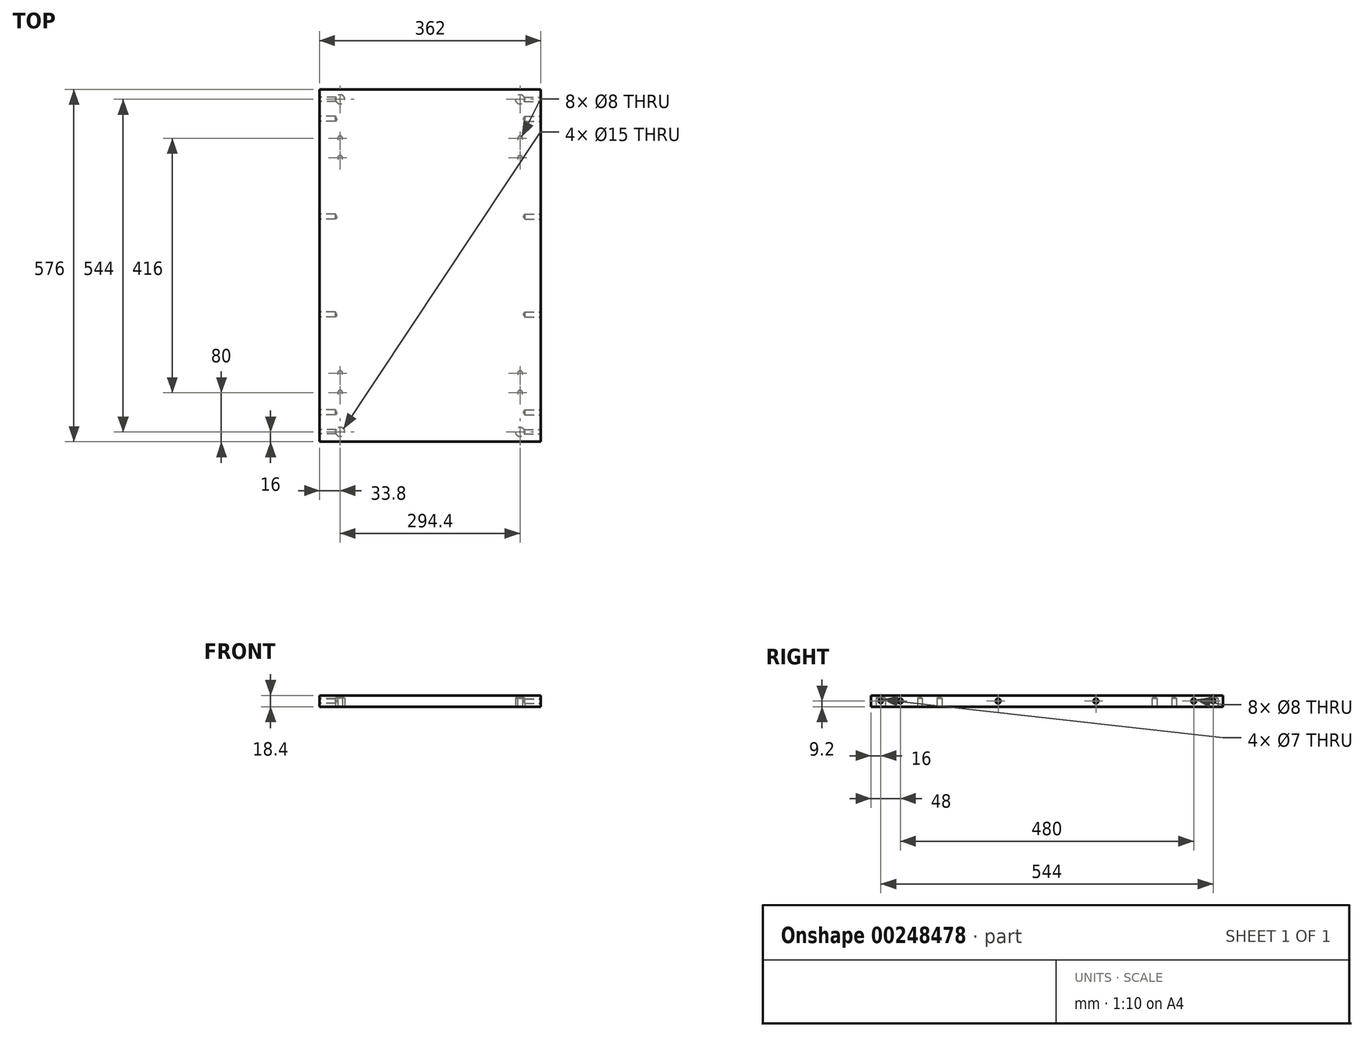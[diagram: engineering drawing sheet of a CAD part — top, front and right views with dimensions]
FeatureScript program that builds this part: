
annotation { "Feature Type Name" : "Feature", "Feature Type Description" : "" }
export const myFeature = defineFeature(function(context is Context, id is Id, definition is map)
    precondition{}
    {
        {
            var Q0;
            Q0=qCreatedBy(makeId("Top.planeOp"),FACE);
            var sketch = newSketch(context, id + "F0", { "sketchPlane" : qUnion([Q0])});
            skLineSegment(sketch, "E0.bottom", {"start": v(0, 0) * mm, "end": v(181, 0) * mm});
            skLineSegment(sketch, "E0.top", {"start": v(0, 288) * mm, "end": v(181, 288) * mm});
            skLineSegment(sketch, "E0.left", {"start": v(0, 0) * mm, "end": v(0, 288) * mm});
            skLineSegment(sketch, "E0.right", {"start": v(181, 0) * mm, "end": v(181, 288) * mm});
            skLineSegment(sketch, "E1.0", {"start": v(147.2, 0) * mm, "end": v(147.2, 288) * mm, "construction": true});
            skPoint(sketch, "E2", {"position": v(147.2, 16) * mm});
            skPoint(sketch, "E3", {"position": v(147.2, 80) * mm});
            skPoint(sketch, "E4", {"position": v(147.2, 112) * mm});
            skSolve(sketch);
        }
        {
            var Q0;
            Q0=makeQuery(id+"F0.imprint","IMPRINT",FACE,{"disambiguationData":[TD([[makeQuery(id+"F0.imprint","IMPRINT",EDGE,{"derivedFrom":sQuery(id+"F0.wireOp",EDGE,"E0.bottom")}),1.0]])]});
            extrude(context, id + "F1", {"entities" : qUnion([Q0]), "depth" : 18.4 * mm});
        }
        {
            var Q0;
            Q0=sQuery(id+"F0.wireOp",VERTEX,"E3");
            var Q1;
            Q1=sQuery(id+"F0.wireOp",VERTEX,"E4");
            var Q2;
            Q2=makeQuery(id+"F1.opExtrude","SWEPT_BODY",BODY,{"disambiguationData":[OSD([sQuery(id+"F0.wireOp",EDGE,"E0.bottom"),sQuery(id+"F0.wireOp",EDGE,"E0.top"),sQuery(id+"F0.wireOp",EDGE,"E0.left"),sQuery(id+"F0.wireOp",EDGE,"E0.right")])]});
            hole(context, id + "F2", {"style" : HoleStyle.SIMPLE, "endStyle" : HoleEndStyle.BLIND, "oppositeDirection" : true, "holeDiameter" : 8 * mm, "holeDepth" : 14 * mm, "tappedDepth" : 12 * mm, "tapClearance" : 3, "startFromSketch" : true, "locations" : qUnion([Q0, Q1]), "scope" : qUnion([Q2])});
        }
        {
            var Q0;
            Q0=sQuery(id+"F0.wireOp",VERTEX,"E2");
            var Q1;
            Q1=makeQuery(id+"F1.opExtrude","SWEPT_BODY",BODY,{"disambiguationData":[OSD([sQuery(id+"F0.wireOp",EDGE,"E0.bottom"),sQuery(id+"F0.wireOp",EDGE,"E0.top"),sQuery(id+"F0.wireOp",EDGE,"E0.left"),sQuery(id+"F0.wireOp",EDGE,"E0.right")])]});
            hole(context, id + "F3", {"style" : HoleStyle.SIMPLE, "endStyle" : HoleEndStyle.BLIND, "oppositeDirection" : true, "holeDiameter" : 15 * mm, "holeDepth" : 14 * mm, "tappedDepth" : 12 * mm, "tapClearance" : 3, "startFromSketch" : true, "locations" : qUnion([Q0]), "scope" : qUnion([Q1])});
        }
        {
            var Q0;
            Q0=makeQuery(id+"F1.opExtrude","SWEPT_FACE",FACE,{"disambiguationData":[OSD([sQuery(id+"F0.wireOp",EDGE,"E0.right")])]});
            var sketch = newSketch(context, id + "F4", { "sketchPlane" : qUnion([Q0])});
            skPoint(sketch, "E5", {"position": v(0, 9.2) * mm});
            skPoint(sketch, "E6", {"position": v(288, 9.2) * mm});
            skLineSegment(sketch, "E7", {"start": v(0, 9.2) * mm, "end": v(288, 9.2) * mm, "construction": true});
            skPoint(sketch, "E8", {"position": v(16, 9.2) * mm});
            skPoint(sketch, "E9", {"position": v(48, 9.2) * mm});
            skPoint(sketch, "E10", {"position": v(208, 9.2) * mm});
            skSolve(sketch);
        }
        {
            var Q0;
            Q0=sQuery(id+"F4.wireOp",VERTEX,"E8");
            var Q1;
            Q1=makeQuery(id+"F1.opExtrude","SWEPT_BODY",BODY,{"disambiguationData":[OSD([sQuery(id+"F0.wireOp",EDGE,"E0.bottom"),sQuery(id+"F0.wireOp",EDGE,"E0.top"),sQuery(id+"F0.wireOp",EDGE,"E0.left"),sQuery(id+"F0.wireOp",EDGE,"E0.right")])]});
            hole(context, id + "F5", {"style" : HoleStyle.SIMPLE, "endStyle" : HoleEndStyle.BLIND, "holeDiameter" : 7 * mm, "holeDepth" : 28 * mm, "tappedDepth" : 12 * mm, "tapClearance" : 3, "startFromSketch" : true, "locations" : qUnion([Q0]), "scope" : qUnion([Q1])});
        }
        {
            var Q0;
            Q0=sQuery(id+"F4.wireOp",VERTEX,"E9");
            var Q1;
            Q1=sQuery(id+"F4.wireOp",VERTEX,"E10");
            var Q2;
            Q2=makeQuery(id+"F1.opExtrude","SWEPT_BODY",BODY,{"disambiguationData":[OSD([sQuery(id+"F0.wireOp",EDGE,"E0.bottom"),sQuery(id+"F0.wireOp",EDGE,"E0.top"),sQuery(id+"F0.wireOp",EDGE,"E0.left"),sQuery(id+"F0.wireOp",EDGE,"E0.right")])]});
            hole(context, id + "F6", {"style" : HoleStyle.SIMPLE, "endStyle" : HoleEndStyle.BLIND, "holeDiameter" : 8 * mm, "holeDepth" : 26 * mm, "tappedDepth" : 12 * mm, "tapClearance" : 3, "startFromSketch" : true, "locations" : qUnion([Q0, Q1]), "scope" : qUnion([Q2])});
        }
        {
            var Q0;
            Q0=makeQuery(id+"F1.opExtrude","SWEPT_BODY",BODY,{"disambiguationData":[OSD([sQuery(id+"F0.wireOp",EDGE,"E0.bottom"),sQuery(id+"F0.wireOp",EDGE,"E0.top"),sQuery(id+"F0.wireOp",EDGE,"E0.left"),sQuery(id+"F0.wireOp",EDGE,"E0.right")])]});
            var Q1;
            Q1=qCreatedBy(makeId("Right.planeOp"),FACE);
            mirror(context, id + "F7", {"operationType" : NewBodyOperationType.ADD, "entities" : qUnion([Q0]), "mirrorPlane" : qUnion([Q1])});
        }
        {
            var Q0;
            Q0=makeQuery(id+"F1.opExtrude","SWEPT_BODY",BODY,{"disambiguationData":[OSD([sQuery(id+"F0.wireOp",EDGE,"E0.bottom"),sQuery(id+"F0.wireOp",EDGE,"E0.top"),sQuery(id+"F0.wireOp",EDGE,"E0.left"),sQuery(id+"F0.wireOp",EDGE,"E0.right")])]});
            var Q1;
            {var subQ0=makeQuery(id+"F1.opExtrude","SWEPT_FACE",FACE,{"disambiguationData":[OSD([sQuery(id+"F0.wireOp",EDGE,"E0.top")])]});Q1=makeQuery(id+"F7.boolean.opBoolean","MERGE",FACE,{"derivedFrom":[subQ0,makeQuery(id+"F7.opPattern","COPY",FACE,{"derivedFrom":subQ0,"instanceName":"1"})]});}
            mirror(context, id + "F8", {"operationType" : NewBodyOperationType.ADD, "entities" : qUnion([Q0]), "mirrorPlane" : qUnion([Q1])});
        }
    });
